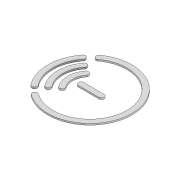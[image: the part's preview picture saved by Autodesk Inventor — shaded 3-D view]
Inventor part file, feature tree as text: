
AUTODESK INVENTOR PART (.ipt)
format: ipt  version: 2020.3 (Build 243373000, 373)  size: 178,176 bytes
history: native  units: mm
features: extrude x1, sketch x1
ambient origin geometry x8: Origin, YZ Plane, XZ Plane, XY Plane, X Axis, Y Axis, Z Axis, Center Point
bodies: Solid1 (feature_tree)
feature tree (2):
  extrude  "Extrusion1"  Depth=6.6mm
  sketch  "Sketch1"  dims[d3=94.5mm d7=6.6mm d8=6.6mm d11=6.0mm d13=6.0mm d29=6.719518mm d30=9.250245mm d31=3.4mm d59=6.6mm d60=3.355485mm d62=3.355mm d63=2.0mm d64=0.0mm]
